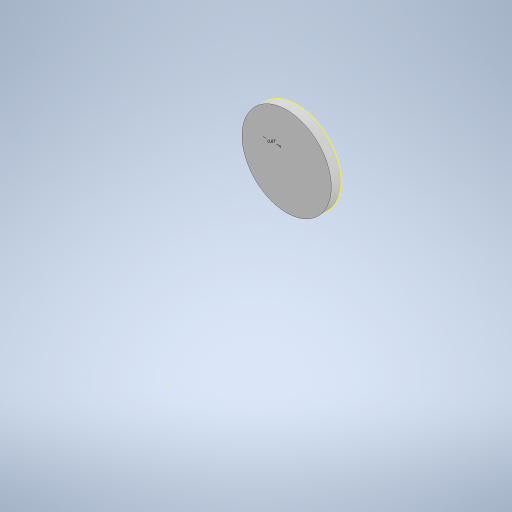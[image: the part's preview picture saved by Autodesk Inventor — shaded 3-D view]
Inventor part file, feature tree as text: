
AUTODESK INVENTOR PART (.ipt)
format: ipt  version: 2023 (Build 270158000, 158)  size: 241,664 bytes
history: native  units: mm
features: other x4, extrude x2, reference x2, plane x1, sketch x1
ambient origin geometry x8: Origin, YZ Plane, XZ Plane, XY Plane, X Axis, Y Axis, Z Axis, Center Point
bodies: Solid1 (feature_tree)
feature tree (10):
  plane  "Work Plane1"
  sketch  "Sketch1"  dims[d0=0.07mm d1=2.0mm d2=0.0mm d3=3.0mm d4=0.0mm]
  extrude  "Extrusion1"  Depth=2.0mm TaperAngle=0.0deg
  extrude  "Extrusion2"  Depth=3.0mm TaperAngle=0.0deg
  reference  "Reference1"
  reference  "Reference2"
  parser-record x1  (decoder bookkeeping rows leaked as tree rows — omitted from the tree; the rows remain in map.json)
  other  "doorLockAssembly_V3.iam"
  other  "pin_V3:1"
  other  "spacerB_V3:1"
note: 1 file-system path scrubbed to <path> (originals preserved in map.json)
